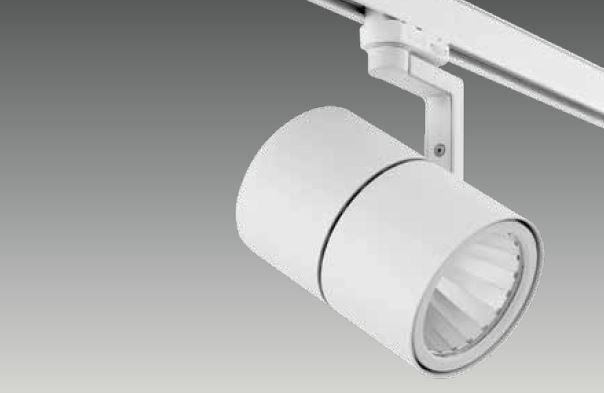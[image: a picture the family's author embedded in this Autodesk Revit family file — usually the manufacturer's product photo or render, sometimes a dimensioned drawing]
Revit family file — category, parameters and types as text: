
# Revit family: DS 1011 PLA (Ra80)
name_source: partatom
category: Lighting Fixtures
revit_build: Autodesk Revit 2017 (Build: 20160225_1515(x64)
units: mm (PartAtom-declared; Revit-internal decimal feet)

## family parameters
Cut with Voids When Loaded = No
Host = Face
Light Source = Yes
Part Type = Normal
Room Calculation Point = No
Round Connector Dimension = Use Diameter
Shared = No

## types (6) — shared parameters
Color Filter = 16777215
Default Elevation = 1219 mm
Dimming Lamp Color Temperature Shift = <None>
Emit Shape Visible in Rendering = Yes
Emit from Circle Diameter = 100 mm  [stored 0.328084 ft]
Light Source Symbol Length = 3048 mm  [stored 10 ft]
Manufacturer = ARLIGHT
Spot Beam Angle = 24.00°
Spot Field Angle = 90.00°
Tilt Angle = 90.00°
Type Image = DS 1011 PLA.JPG

## per-type parameters (varying)
| type | Wattage Comments |
| DSPLA.11.19.30.24.80 | 19 |
| DSPLA.11.19.40.24.80 | 19 |
| DSPLA.11.27.30.24.80 | 27 |
| DSPLA.11.27.40.24.80 | 27 |
| DSPLA.11.35.30.24.80 | 35 |
| DSPLA.11.35.40.24.80 | 35 |

note: [stored X ft] marks values corroborated as IEEE doubles in the binary element streams (Revit-internal decimal feet)

## geometry (parser evidence)
native form markers: Sweep x3
no freeform markers — native parametric forms only
